# Revit family: Storage-Teknion-LWBRW_Byward_Return_Wall_Mounted-R2019
name_source: partatom
category: Furniture
units: mm (PartAtom-declared; Revit-internal decimal feet)

## family parameters
Always vertical = Yes
Cut with Voids When Loaded = No
OmniClass Number = 23.40.20.00
OmniClass Title = General Furniture and Specialties
Room Calculation Point = No
Shared = Yes
Work Plane-Based = No

## types (6) — shared parameters
Assembly Code = E2020200
Manufacturer = Teknion
Manufacturer Fax = 416.661.4586
Part Number = LWBRW
Product Documentation Link = https://assets.teknion.com
Product Line = Byward
Product Page URL = https://www.teknion.com
Series = Byward
Sustainability Data = https://www.teknion.com
URL = www.teknion.com
Unit Weight URL = http://www.teknion.com
Warranty = http://www.teknion.com

## per-type parameters (varying)
| type | Description | Inset lower box offset | Model | Width |
| 14" Depth, 36" Width, Flush lower box | Byward Return, Wall Mounted, 14" Depth, 36" Width, Flush lower box | 0 " | LWBRW1436F_ | 36 " |
| 14" Depth, 36" Width, Inset lower box | Byward Return, Wall Mounted, 14" Depth, 36" Width, Inset lower box | 3.06 " | LWBRW1436I_ | 36 " |
| 14" Depth, 42" Width, Inset lower box | Byward Return, Wall Mounted, 14" Depth, 42" Width, Inset lower box | 3.06 " | LWBRW1442I_ | 42 " |
| 14" Depth, 48" Width, Inset lower box | Byward Return, Wall Mounted, 14" Depth, 48" Width, Inset lower box | 3.06 " | LWBRW1448I_ | 48 " |
| 14" Depth, 42" Width, Flush lower box | Byward Return, Wall Mounted, 14" Depth, 42" Width, Flush lower box | 0 " | LWBRW1442F_ | 42 " |
| 14" Depth, 48" Width, Flush lower box | Byward Return, Wall Mounted, 14" Depth, 48" Width, Flush lower box | 0 " | LWBRW1448F_ | 48 " |

## geometry (parser evidence)
native form markers: Sweep x2
no freeform markers — native parametric forms only
